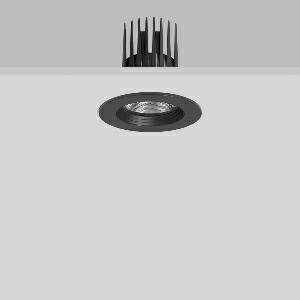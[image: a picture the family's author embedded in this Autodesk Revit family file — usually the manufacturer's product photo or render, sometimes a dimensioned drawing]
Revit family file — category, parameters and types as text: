
# Revit family: heledon_mini_e_901749_003_1_2652
name_source: partatom
category: Lighting Fixtures
units: mm (PartAtom-declared; Revit-internal decimal feet)

## family parameters
Cut with Voids When Loaded = No
Host = Face
Light Source = No
Part Type = Normal
Room Calculation Point = No
Round Connector Dimension = Use Diameter
Shared = No

## types (1)
- HELEDON mini E (1 x LED Modul 940, 3700 lm, 4000)
    Apparent Load = 29 VA
    Approval mark = CE
    CIE Flux Codes = 99 100 100 100 100
    Color Rendering = 92
    Color Temperature = 4000
    Default Elevation = 1800 mm
    Description = Series: HELEDON mini
Round recessed downlight. Housing: die-cast aluminium, powder-coated. Black plastic ring and recessed LED to prevent glare from the side. Optical assembly with reflector made of MIRO-Silver with 98% total light reflection for outstanding efficiency - can be changed without tools. Best colour rendering index Ra>90. Suitable for Recessed ceiling mounting. Installation without tools thanks to spring fastening system. Including separate LED converter with connecting cable 600 mm.High quality converter without flickering and stroboscopic effect. Through-wiring box (5 pole) available as accessory. The following accessories can be mounted without use of tools: interchangeable lenses, decorative glasses, honeycomb louvre, clear and frosted diffusers, white interchangeable plastic ring. 
Colour: deep black, matt (RAL 9005)
Diameter: 124 mm
Height: 3 mm
Cut-out diameter: 114 mm
Recess height: 170 mm
Luminaire: recess height: 120 mm
Lamp: LED
Socket: without socket
Colour temperature: 4000K
Colour rendering index (CRI): 92
System power: 29 W
Rated luminous flux: 3700 lm
Luminous efficiency: 128 lm/W
Control gear: Regulated power supply
Protection class: II
Type of protection: IP 20
    Height = 0 mm  [stored 0 ft]
    Lamp = 1 x LED Modul 940
    Lamp Light Flux = 3700 lm
    Lamp count = 1
    Length = 124 mm  [stored 0.406824 ft]
    Lifetime = 50000 h
    Luminous efficacy = 128 lm/W
    Manufacturer = RZB
    ModVariant = No
    Model = 901749.003.1
    Mounting Place = Ceiling
    Mounting Type = Recessed
    Number of Poles = 1
    OnlyDefault = Yes
    Power Factor = 1
    Product Name = HELEDON mini E
    Product group = Recessed downlights
    ProductGroupID = 402
    Protection Class = Protection class II
    Protection Degree = IP 20
    RLX_Detail_Level = 1
    RLX_Emergency_Light_Flux = 0 lm
    RLX_Emergency_Type = 0
    RLX_Emergency_Type_DB = No
    RlxData = <blob elided: 126825 chars, md5=9f2d75a0>
    Socket = socket
    Standby Power = 0 W
    System Light Flux = 3700 lm
    System Power = 29 W
    Type Comments = Product without accessories
    Type Image = 901657.003.jpg
    URL = http://relux.com
    VarID = ---
    Voltage = 230 V
    Voltage Range = 220-240 V
    Weight = 0.00 kg
    Width = 0 mm  [stored 0 ft]

note: [stored X ft] marks values corroborated as IEEE doubles in the binary element streams (Revit-internal decimal feet)

## geometry (parser evidence)
native form markers: Blend x4, Sweep x12
no freeform markers — native parametric forms only
